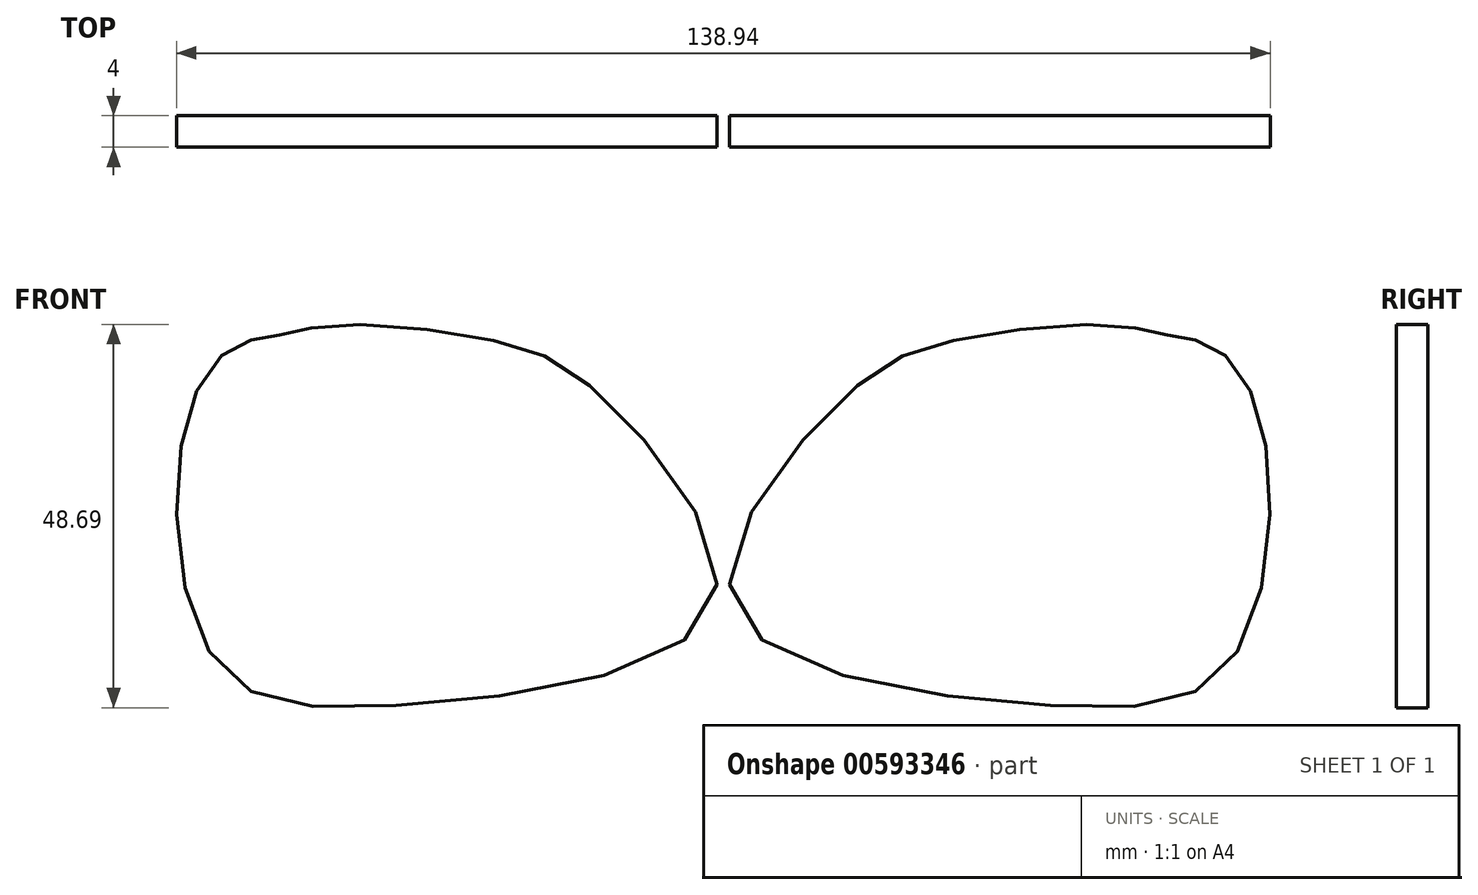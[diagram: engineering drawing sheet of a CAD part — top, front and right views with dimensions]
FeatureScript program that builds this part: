
annotation { "Feature Type Name" : "Feature", "Feature Type Description" : "" }
export const myFeature = defineFeature(function(context is Context, id is Id, definition is map)
    precondition{}
    {
        {
            var Q0;
            Q0=qCreatedBy(makeId("Front.planeOp"),FACE);
            var sketch = newSketch(context, id + "F0", { "sketchPlane" : qUnion([Q0])});
            skFitSpline(sketch, "E0", {"points": [v(21.03, 16.18) * mm, v(-5.48, 14.14) * mm, v(-19.24, 5.99) * mm, v(-25.36, -13.89) * mm, v(4.71, -28.16) * mm, v(26.12, -23.06) * mm, v(32.75, -3.7) * mm, v(29.18, 11.09) * mm, v(21.03, 16.18) * mm]});
            skSolve(sketch);
        }
        {
            var Q0;
            Q0=qCreatedBy(makeId("Front.planeOp"),FACE);
            var sketch = newSketch(context, id + "F1", { "sketchPlane" : qUnion([Q0])});
            skFitSpline(sketch, "E1.0", {"points": [v(21.03, 16.18) * mm, v(14.22, 17.4) * mm, v(-6.73, 15.23) * mm, v(-19.71, 8.16) * mm, v(-33.73, -18.07) * mm, v(5.24, -30.87) * mm, v(28.48, -26.55) * mm, v(34.45, -3.9) * mm, v(30.29, 11.84) * mm, v(25.12, 15.46) * mm, v(21.03, 16.18) * mm]});
            skLineSegment(sketch, "E2", {"start": v(-35, 39.12) * mm, "end": v(-35, -64.86) * mm, "construction": true});
            skFitSpline(sketch, "E3.MirrorC", {"points": [v(-91.03, 16.18) * mm, v(-84.22, 17.4) * mm, v(-63.27, 15.23) * mm, v(-50.29, 8.16) * mm, v(-36.27, -18.07) * mm, v(-75.24, -30.87) * mm, v(-98.48, -26.55) * mm, v(-104.45, -3.9) * mm, v(-100.29, 11.84) * mm, v(-95.12, 15.46) * mm, v(-91.03, 16.18) * mm]});
            skFitSpline(sketch, "E4.0", {"points": [v(24.54, 20.54) * mm, v(21.93, 21.15) * mm, v(19.13, 21.5) * mm, v(15.17, 21.72) * mm, v(9.83, 21.6) * mm, v(4.3, 21.04) * mm, v(0, 20.4) * mm, v(-3.12, 19.83) * mm, v(-6.08, 19.17) * mm, v(-8.81, 18.44) * mm, v(-11.39, 17.58) * mm, v(-13.83, 16.55) * mm, v(-16.15, 15.3) * mm, v(-18.33, 13.82) * mm, v(-20.38, 12.1) * mm, v(-21.98, 10.47) * mm, v(-23.21, 9.05) * mm, v(-24.44, 7.54) * mm, v(-25.93, 5.48) * mm, v(-27.6, 2.77) * mm, v(-29.07, -0.16) * mm, v(-30.26, -3.3) * mm, v(-31.05, -6.61) * mm, v(-31.27, -9.53) * mm, v(-31.07, -11.94) * mm, v(-30.77, -13.45) * mm, v(-30.42, -14.65) * mm, v(-30.1, -15.55) * mm, v(-29.7, -16.43) * mm, v(-29.12, -17.56) * mm, v(-28.28, -18.88) * mm, v(-26.73, -20.82) * mm, v(-24.48, -22.95) * mm, v(-21.42, -25.11) * mm, v(-18.08, -26.97) * mm, v(-14.5, -28.57) * mm, v(-10.78, -29.93) * mm, v(-6.95, -31.07) * mm, v(-3.1, -32) * mm, v(0.73, -32.7) * mm, v(4.44, -33.2) * mm, v(8, -33.48) * mm, v(11.44, -33.52) * mm, v(15.85, -33.25) * mm, v(20, -32.4) * mm, v(23.85, -30.85) * mm, v(26.55, -29.3) * mm, v(28.59, -27.68) * mm, v(30.07, -26.2) * mm, v(31.43, -24.62) * mm, v(32.9, -22.5) * mm, v(34.35, -19.78) * mm, v(35.51, -16.93) * mm, v(36.71, -13.02) * mm, v(37.63, -8.02) * mm, v(37.87, -2.1) * mm, v(37.4, 2.53) * mm, v(36.67, 6) * mm, v(35.95, 8.45) * mm, v(35.05, 10.77) * mm, v(34.14, 12.56) * mm, v(33.33, 13.9) * mm, v(32.43, 15.2) * mm, v(31.11, 16.74) * mm, v(29.19, 18.36) * mm, v(26.97, 19.63) * mm, v(24.54, 20.54) * mm, v(21.93, 21.15) * mm, v(19.13, 21.5) * mm, v(24.54, 20.54) * mm]});
            skFitSpline(sketch, "E5.0", {"points": [v(-94.54, 20.54) * mm, v(-91.93, 21.15) * mm, v(-89.13, 21.5) * mm, v(-85.17, 21.72) * mm, v(-79.83, 21.6) * mm, v(-74.3, 21.04) * mm, v(-70, 20.4) * mm, v(-66.88, 19.83) * mm, v(-63.92, 19.17) * mm, v(-61.19, 18.44) * mm, v(-58.61, 17.58) * mm, v(-56.17, 16.55) * mm, v(-53.85, 15.3) * mm, v(-51.67, 13.82) * mm, v(-49.62, 12.1) * mm, v(-48.02, 10.47) * mm, v(-46.79, 9.05) * mm, v(-45.56, 7.54) * mm, v(-44.07, 5.48) * mm, v(-42.4, 2.77) * mm, v(-40.93, -0.16) * mm, v(-39.74, -3.3) * mm, v(-38.95, -6.61) * mm, v(-38.73, -9.53) * mm, v(-38.93, -11.94) * mm, v(-39.23, -13.45) * mm, v(-39.58, -14.65) * mm, v(-39.9, -15.55) * mm, v(-40.3, -16.43) * mm, v(-40.88, -17.56) * mm, v(-41.72, -18.88) * mm, v(-43.27, -20.82) * mm, v(-45.52, -22.95) * mm, v(-48.58, -25.11) * mm, v(-51.92, -26.97) * mm, v(-55.5, -28.57) * mm, v(-59.22, -29.93) * mm, v(-63.05, -31.07) * mm, v(-66.9, -32) * mm, v(-70.73, -32.7) * mm, v(-74.44, -33.2) * mm, v(-78, -33.48) * mm, v(-81.44, -33.52) * mm, v(-85.85, -33.25) * mm, v(-90, -32.4) * mm, v(-93.85, -30.85) * mm, v(-96.55, -29.3) * mm, v(-98.59, -27.68) * mm, v(-100.07, -26.2) * mm, v(-101.43, -24.62) * mm, v(-102.9, -22.5) * mm, v(-104.35, -19.78) * mm, v(-105.51, -16.93) * mm, v(-106.71, -13.02) * mm, v(-107.63, -8.02) * mm, v(-107.87, -2.1) * mm, v(-107.4, 2.53) * mm, v(-106.67, 6) * mm, v(-105.95, 8.45) * mm, v(-105.05, 10.77) * mm, v(-104.14, 12.56) * mm, v(-103.33, 13.9) * mm, v(-102.43, 15.2) * mm, v(-101.11, 16.74) * mm, v(-99.19, 18.36) * mm, v(-96.97, 19.63) * mm, v(-94.54, 20.54) * mm, v(-91.93, 21.15) * mm, v(-89.13, 21.5) * mm, v(-94.54, 20.54) * mm]});
            skFitSpline(sketch, "E6", {"points": [v(-21.78, 10.64) * mm, v(-29.08, 6.73) * mm, v(-35, 5.87) * mm], "startDerivative": vector(-11.5, -13.27) * mm, "endDerivative": vector(-14.7, 0.5) * mm});
            skFitSpline(sketch, "E7", {"points": [v(-31.1, -7.76) * mm, v(-32.5, -5.7) * mm, v(-35, -5.29) * mm], "startDerivative": vector(1, 7.63) * mm, "endDerivative": vector(-6.9, 0.35) * mm});
            skFitSpline(sketch, "E8.MirrorCS", {"points": [v(-48.22, 10.64) * mm, v(-40.92, 6.73) * mm, v(-35, 5.87) * mm], "startDerivative": vector(11.5, -13.27) * mm, "endDerivative": vector(14.7, 0.5) * mm});
            skFitSpline(sketch, "E9.MirrorCS", {"points": [v(-38.9, -7.76) * mm, v(-37.5, -5.7) * mm, v(-35, -5.29) * mm], "startDerivative": vector(-1, 7.63) * mm, "endDerivative": vector(6.9, 0.35) * mm});
            skSolve(sketch);
        }
        {
            var Q0;
            Q0 = qSketchRegion(id + "F1", true);
            extrude(context, id + "F2", {"entities" : qUnion([Q0]), "depth" : 4 * mm, "offsetDistance" : 25 * mm});
        }
    });
